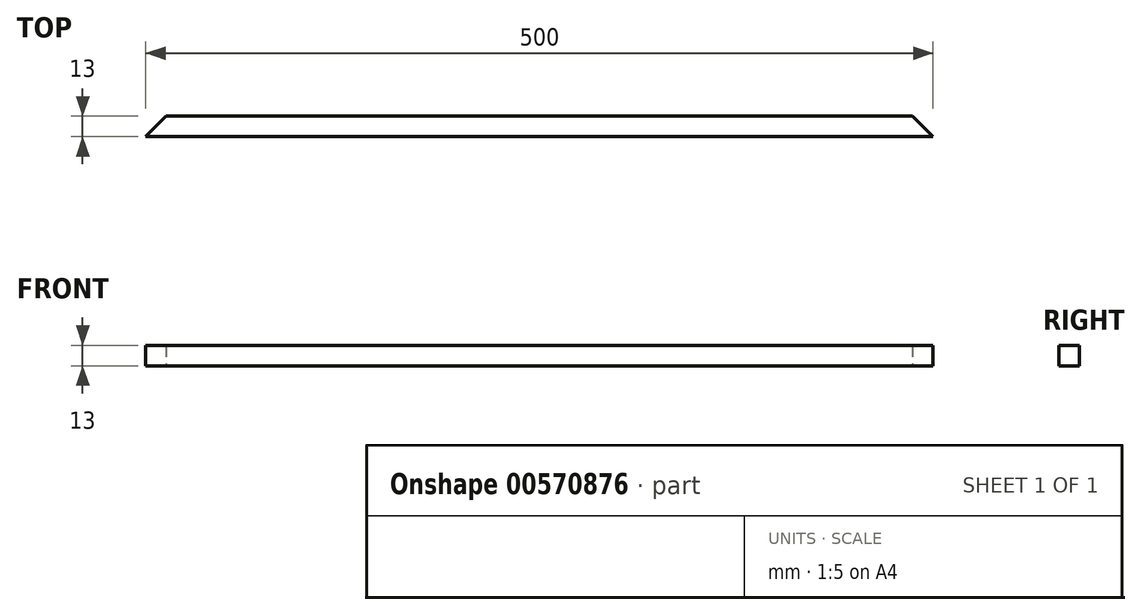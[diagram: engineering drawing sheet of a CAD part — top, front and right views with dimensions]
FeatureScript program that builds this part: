
annotation { "Feature Type Name" : "Feature", "Feature Type Description" : "" }
export const myFeature = defineFeature(function(context is Context, id is Id, definition is map)
    precondition{}
    {
        {
            var Q0;
            Q0=qCreatedBy(makeId("Top.planeOp"),FACE);
            var sketch = newSketch(context, id + "F0", { "sketchPlane" : qUnion([Q0])});
            skLineSegment(sketch, "E0.bottom", {"start": v(-250, 0) * mm, "end": v(250, 0) * mm});
            skLineSegment(sketch, "E0.top", {"start": v(-237, 13) * mm, "end": v(237, 13) * mm});
            skLineSegment(sketch, "E1", {"start": v(-250, 0) * mm, "end": v(-237, 13) * mm});
            skLineSegment(sketch, "E2", {"start": v(250, 0) * mm, "end": v(237, 13) * mm});
            skSolve(sketch);
        }
        {
            var Q0;
            Q0=makeQuery(id+"F0.imprint","IMPRINT",FACE,{"disambiguationData":[TD([[makeQuery(id+"F0.imprint","IMPRINT",EDGE,{"derivedFrom":sQuery(id+"F0.wireOp",EDGE,"E0.bottom")}),1.0]])]});
            extrude(context, id + "F1", {"entities" : qUnion([Q0]), "depth" : 13 * mm, "offsetDistance" : 25 * mm});
        }
    });
